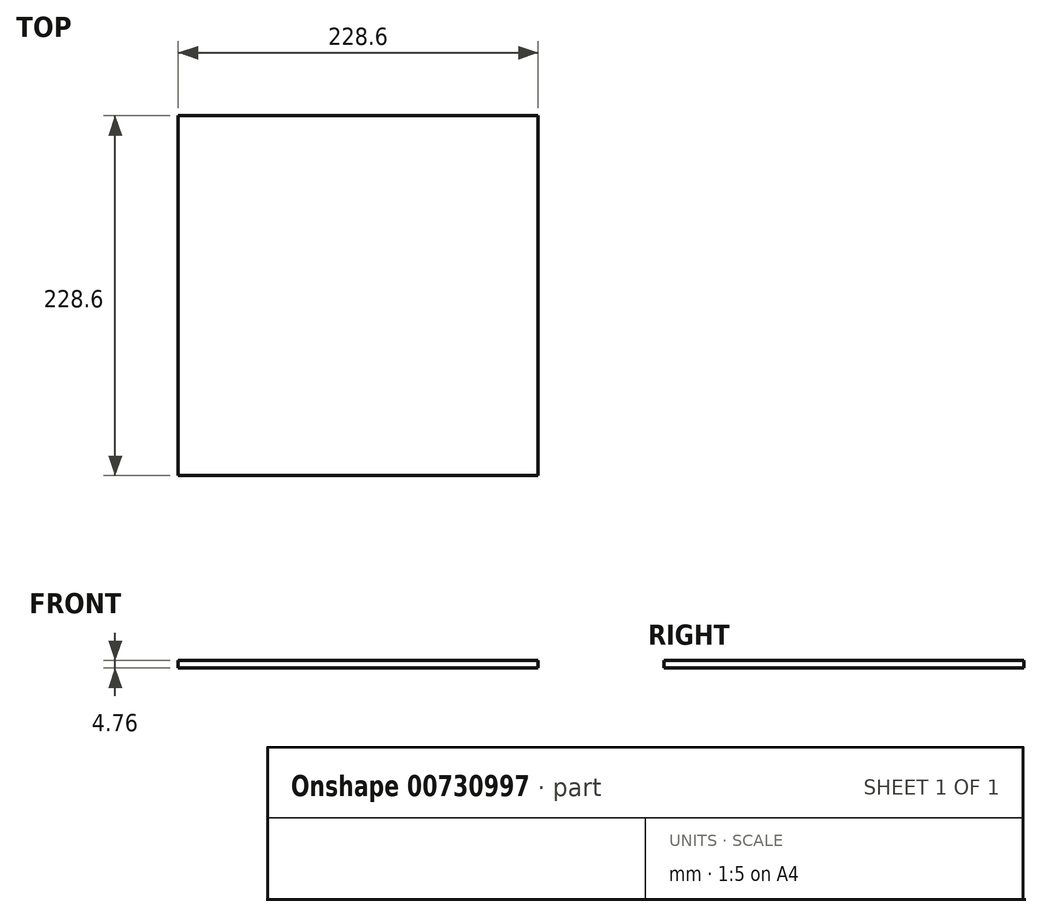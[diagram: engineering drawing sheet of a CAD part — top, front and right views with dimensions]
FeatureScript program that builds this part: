
annotation { "Feature Type Name" : "Feature", "Feature Type Description" : "" }
export const myFeature = defineFeature(function(context is Context, id is Id, definition is map)
    precondition{}
    {
        {
            var Q0;
            Q0=qCreatedBy(makeId("Top.planeOp"),FACE);
            var sketch = newSketch(context, id + "F0", { "sketchPlane" : qUnion([Q0])});
            skLineSegment(sketch, "E0.bottom", {"start": v(114.3, -114.3) * mm, "end": v(-114.3, -114.3) * mm});
            skLineSegment(sketch, "E0.top", {"start": v(114.3, 114.3) * mm, "end": v(-114.3, 114.3) * mm});
            skLineSegment(sketch, "E0.left", {"start": v(114.3, -114.3) * mm, "end": v(114.3, 114.3) * mm});
            skLineSegment(sketch, "E0.right", {"start": v(-114.3, -114.3) * mm, "end": v(-114.3, 114.3) * mm});
            skPoint(sketch, "E0.middle", {"position": v(0, 0) * mm});
            skSolve(sketch);
        }
        {
            var Q0;
            Q0=makeQuery(id+"F0.imprint","IMPRINT",FACE,{"disambiguationData":[TD([[makeQuery(id+"F0.imprint","IMPRINT",EDGE,{"derivedFrom":sQuery(id+"F0.wireOp",EDGE,"E0.bottom")}),-1.0]])]});
            extrude(context, id + "F1", {"entities" : qUnion([Q0]), "depth" : 4.76 * mm, "offsetDistance" : 25.4 * mm});
        }
    });
